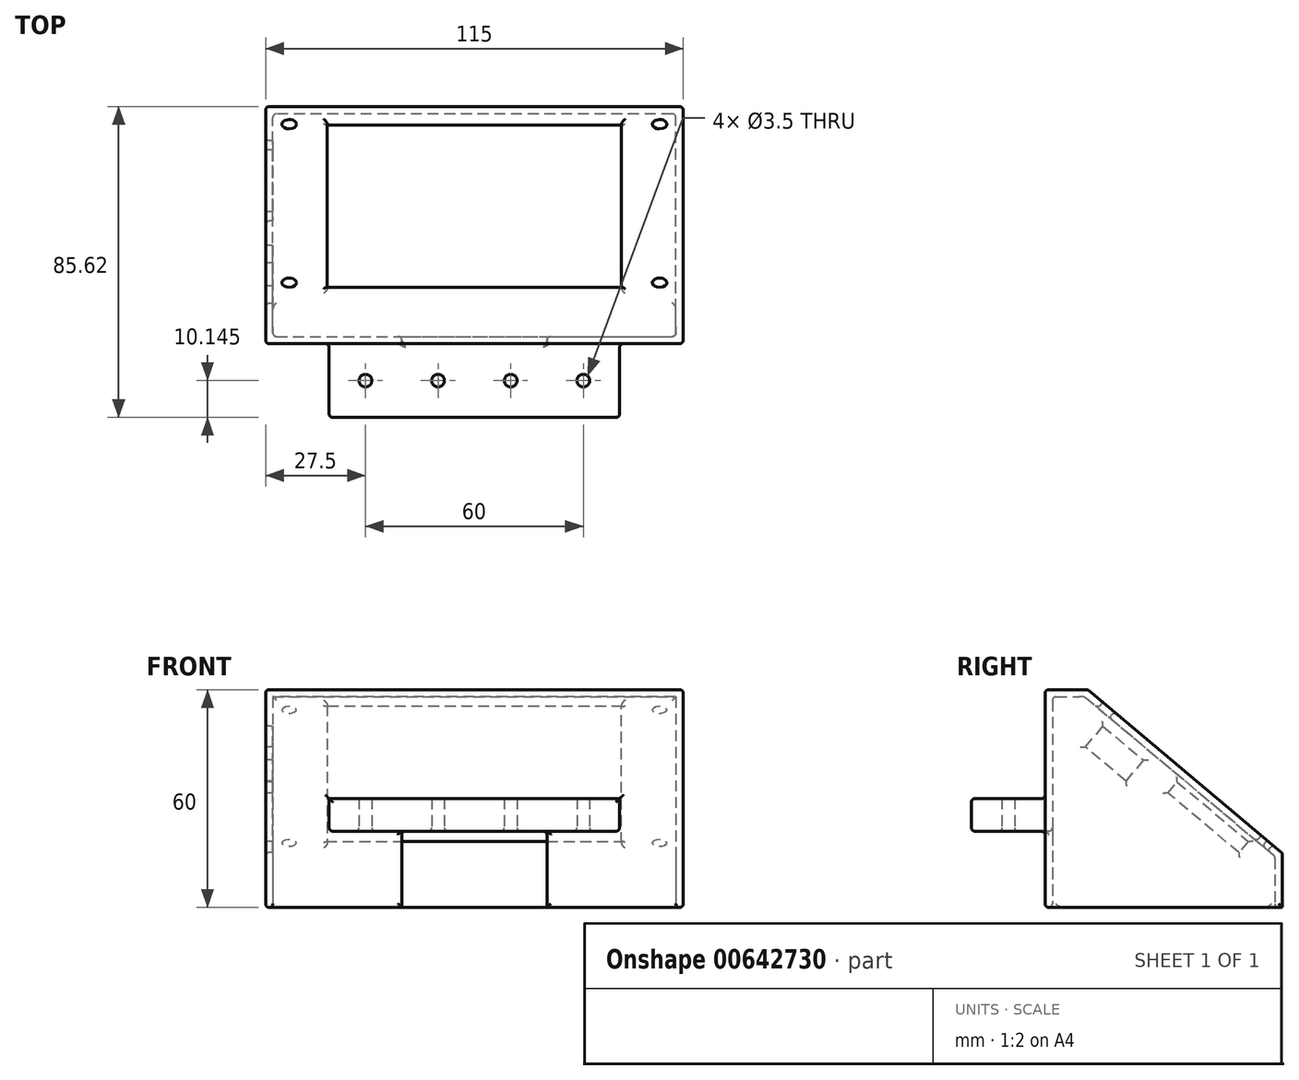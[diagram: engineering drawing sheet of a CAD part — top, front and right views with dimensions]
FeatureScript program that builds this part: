
annotation { "Feature Type Name" : "Feature", "Feature Type Description" : "" }
export const myFeature = defineFeature(function(context is Context, id is Id, definition is map)
    precondition{}
    {
        {
            var Q0;
            Q0=qCreatedBy(makeId("Right.planeOp"),FACE);
            var sketch = newSketch(context, id + "F0", { "sketchPlane" : qUnion([Q0])});
            skLineSegment(sketch, "E0.bottom", {"start": v(-40.36, -2.42) * mm, "end": v(-8.36, -2.42) * mm});
            skLineSegment(sketch, "E0.top", {"start": v(-40.36, -62.42) * mm, "end": v(45.26, -62.42) * mm});
            skLineSegment(sketch, "E0.left", {"start": v(-40.36, -2.42) * mm, "end": v(-40.36, -62.42) * mm});
            skLineSegment(sketch, "E0.right", {"start": v(45.26, -47.41) * mm, "end": v(45.26, -62.42) * mm});
            skLineSegment(sketch, "E1", {"start": v(-8.36, -2.42) * mm, "end": v(45.26, -47.41) * mm});
            skLineSegment(sketch, "E2.bottom", {"start": v(-40.36, -12.12) * mm, "end": v(-20.06, -12.12) * mm});
            skLineSegment(sketch, "E2.top", {"start": v(-40.36, -32.42) * mm, "end": v(-20.06, -32.42) * mm});
            skLineSegment(sketch, "E2.left", {"start": v(-40.36, -12.12) * mm, "end": v(-40.36, -32.42) * mm});
            skLineSegment(sketch, "E2.right", {"start": v(-20.06, -12.12) * mm, "end": v(-20.06, -32.42) * mm});
            skSolve(sketch);
        }
        {
            var Q0;
            {var subQ4=sQuery(id+"F0.wireOp",EDGE,"E0.bottom");Q0=makeQuery(id+"F0.imprint","IMPRINT",FACE,{"disambiguationData":[TD([[makeQuery(id+"F0.imprint","IMPRINT",EDGE,{"derivedFrom":subQ4}),-1.0]])]});}
            extrude(context, id + "F1", {"entities" : qUnion([Q0]), "depth" : 115 * mm, "offsetDistance" : 25 * mm});
        }
        {
            var Q0;
            Q0=makeQuery(id+"F1.opExtrude","CAP_FACE",FACE,{"disambiguationData":[OSD([sQuery(id+"F0.wireOp",EDGE,"E0.bottom"),sQuery(id+"F0.wireOp",EDGE,"E0.top"),sQuery(id+"F0.wireOp",EDGE,"E0.left"),sQuery(id+"F0.wireOp",EDGE,"E0.right"),sQuery(id+"F0.wireOp",EDGE,"E1"),sQuery(id+"F0.wireOp",EDGE,"E2.bottom"),sQuery(id+"F0.wireOp",EDGE,"E2.top"),sQuery(id+"F0.wireOp",EDGE,"E2.right")])],"isStart":false});
            var sketch = newSketch(context, id + "F2", { "sketchPlane" : qUnion([Q0])});
            skLineSegment(sketch, "E3", {"start": v(-20.06, -12.12) * mm, "end": v(-20.06, -2.42) * mm});
            skLineSegment(sketch, "E4", {"start": v(-20.06, -32.42) * mm, "end": v(-20.06, -62.42) * mm});
            skSolve(sketch);
        }
        {
            var Q0;
            {var subQ0=sQuery(id+"F2.wireOp",EDGE,"E3");Q0=makeQuery(id+"F2.imprint","IMPRINT",FACE,{"disambiguationData":[TD([[makeQuery(id+"F2.imprint","IMPRINT",EDGE,{"derivedFrom":subQ0}),1.0]])]});}
            var Q1;
            {var subQ0=sQuery(id+"F2.wireOp",EDGE,"E4");Q1=makeQuery(id+"F2.imprint","IMPRINT",FACE,{"disambiguationData":[TD([[makeQuery(id+"F2.imprint","IMPRINT",EDGE,{"derivedFrom":subQ0}),-1.0]])]});}
            extrude(context, id + "F3", {"entities" : qUnion([Q0, Q1]), "operationType" : NewBodyOperationType.REMOVE, "oppositeDirection" : true, "depth" : 17.5 * mm, "offsetDistance" : 25 * mm});
        }
        {
            var Q0;
            Q0=makeQuery(id+"F1.opExtrude","CAP_FACE",FACE,{"disambiguationData":[OSD([sQuery(id+"F0.wireOp",EDGE,"E0.bottom"),sQuery(id+"F0.wireOp",EDGE,"E0.top"),sQuery(id+"F0.wireOp",EDGE,"E0.left"),sQuery(id+"F0.wireOp",EDGE,"E0.right"),sQuery(id+"F0.wireOp",EDGE,"E1"),sQuery(id+"F0.wireOp",EDGE,"E2.bottom"),sQuery(id+"F0.wireOp",EDGE,"E2.top"),sQuery(id+"F0.wireOp",EDGE,"E2.right")])],"isStart":true});
            var sketch = newSketch(context, id + "F4", { "sketchPlane" : qUnion([Q0])});
            skLineSegment(sketch, "E5", {"start": v(20.06, -12.12) * mm, "end": v(20.06, -2.42) * mm});
            skLineSegment(sketch, "E6", {"start": v(20.06, -32.42) * mm, "end": v(20.06, -62.42) * mm});
            skSolve(sketch);
        }
        {
            var Q0;
            {var subQ0=sQuery(id+"F4.wireOp",EDGE,"E5");Q0=makeQuery(id+"F4.imprint","IMPRINT",FACE,{"disambiguationData":[TD([[makeQuery(id+"F4.imprint","IMPRINT",EDGE,{"derivedFrom":subQ0}),-1.0]])]});}
            var Q1;
            {var subQ0=sQuery(id+"F4.wireOp",EDGE,"E6");Q1=makeQuery(id+"F4.imprint","IMPRINT",FACE,{"disambiguationData":[TD([[makeQuery(id+"F4.imprint","IMPRINT",EDGE,{"derivedFrom":subQ0}),1.0]])]});}
            extrude(context, id + "F5", {"entities" : qUnion([Q0, Q1]), "operationType" : NewBodyOperationType.REMOVE, "oppositeDirection" : true, "depth" : 17.5 * mm, "offsetDistance" : 25 * mm});
        }
        {
            var Q0;
            Q0=makeQuery(id+"F1.opExtrude","SWEPT_FACE",FACE,{"disambiguationData":[OSD([sQuery(id+"F0.wireOp",EDGE,"E0.top")])]});
            var sketch = newSketch(context, id + "F6", { "sketchPlane" : qUnion([Q0])});
            skLineSegment(sketch, "E7", {"start": v(17.5, 20.06) * mm, "end": v(97.5, 20.06) * mm});
            skSolve(sketch);
        }
        {
            var Q0;
            Q0=makeQuery(id+"F6.imprint","IMPRINT",FACE,{"disambiguationData":[TD([[makeQuery(id+"F6.imprint","IMPRINT",EDGE,{"derivedFrom":sQuery(id+"F6.wireOp",EDGE,"E7")}),1.0]])]});
            extrude(context, id + "F7", {"entities" : qUnion([Q0]), "operationType" : NewBodyOperationType.REMOVE, "oppositeDirection" : true, "depth" : 21 * mm, "offsetDistance" : 25 * mm});
        }
        {
            var Q0;
            Q0=makeQuery(id+"F1.opExtrude","SWEPT_FACE",FACE,{"disambiguationData":[OSD([sQuery(id+"F0.wireOp",EDGE,"E0.top")])]});
            shell(context, id + "F8", {"entities" : qUnion([Q0]), "thickness" : 2 * mm});
        }
        {
            var Q0;
            {var subQ0=sQuery(id+"F0.wireOp",EDGE,"E0.left");Q0=makeQuery(id+"F1.opExtrude","SWEPT_FACE",FACE,{"disambiguationData":[OSD([subQ0]),TDD([makeQuery(id+"F0.imprint","IMPRINT",EDGE,{"disambiguationData":[TD([[makeQuery(id+"F0.imprint","INTERSECT",VERTEX,{"derivedFrom":[sQuery(id+"F0.wireOp",EDGE,"E0.bottom"),subQ0]}),-1.0]])],"derivedFrom":subQ0})])]});}
            var Q1;
            {var subQ0=sQuery(id+"F0.wireOp",EDGE,"E0.left");Q1=makeQuery(id+"F1.opExtrude","SWEPT_FACE",FACE,{"disambiguationData":[OSD([subQ0]),TDD([makeQuery(id+"F0.imprint","IMPRINT",EDGE,{"disambiguationData":[TD([[makeQuery(id+"F0.imprint","INTERSECT",VERTEX,{"derivedFrom":[sQuery(id+"F0.wireOp",EDGE,"E0.top"),subQ0]}),1.0]])],"derivedFrom":subQ0})])]});}
            var Q2;
            Q2=makeQuery(id+"F8.opShell","OFFSET_FACE",FACE,{"disambiguationData":[OSD([sQuery(id+"F0.wireOp",EDGE,"E2.right"),sQuery(id+"F2.wireOp",EDGE,"E3"),sQuery(id+"F2.wireOp",EDGE,"E4"),sQuery(id+"F4.wireOp",EDGE,"E5"),sQuery(id+"F4.wireOp",EDGE,"E6"),sQuery(id+"F6.wireOp",EDGE,"E7")])]});
            extrude(context, id + "F9", {"entities" : qUnion([Q0, Q1]), "operationType" : NewBodyOperationType.ADD, "endBound" : BoundingType.UP_TO_SURFACE, "oppositeDirection" : true, "depth" : 25 * mm, "endBoundEntityFace" : qUnion([Q2]), "offsetDistance" : 25 * mm});
        }
        {
            var Q0;
            Q0=makeQuery(id+"F7.boolean.opBoolean","MERGE",FACE,{"derivedFrom":[makeQuery(id+"F5.boolean.opBoolean","MERGE",FACE,{"derivedFrom":[makeQuery(id+"F3.boolean.opBoolean","MERGE",FACE,{"derivedFrom":[makeQuery(id+"F1.opExtrude","SWEPT_FACE",FACE,{"disambiguationData":[OSD([sQuery(id+"F0.wireOp",EDGE,"E2.right")])]}),makeQuery(id+"F3.opExtrude","SWEPT_FACE",FACE,{"disambiguationData":[OSD([sQuery(id+"F2.wireOp",EDGE,"E3")])]}),makeQuery(id+"F3.opExtrude","SWEPT_FACE",FACE,{"disambiguationData":[OSD([sQuery(id+"F2.wireOp",EDGE,"E4")])]})]}),makeQuery(id+"F5.opExtrude","SWEPT_FACE",FACE,{"disambiguationData":[OSD([sQuery(id+"F4.wireOp",EDGE,"E5")])]}),makeQuery(id+"F5.opExtrude","SWEPT_FACE",FACE,{"disambiguationData":[OSD([sQuery(id+"F4.wireOp",EDGE,"E6")])]})]}),makeQuery(id+"F7.opExtrude","SWEPT_FACE",FACE,{"disambiguationData":[OSD([sQuery(id+"F6.wireOp",EDGE,"E7")])]})]});
            var sketch = newSketch(context, id + "F10", { "sketchPlane" : qUnion([Q0])});
            skLineSegment(sketch, "E8.bottom", {"start": v(77.5, -41.42) * mm, "end": v(37.5, -41.42) * mm});
            skLineSegment(sketch, "E8.top", {"start": v(77.5, -83.42) * mm, "end": v(37.5, -83.42) * mm});
            skLineSegment(sketch, "E8.left", {"start": v(77.5, -41.42) * mm, "end": v(77.5, -83.42) * mm});
            skLineSegment(sketch, "E8.right", {"start": v(37.5, -41.42) * mm, "end": v(37.5, -83.42) * mm});
            skPoint(sketch, "E8.middle", {"position": v(57.5, -62.42) * mm});
            skSolve(sketch);
        }
        {
            var Q0;
            {var subQ0=sQuery(id+"F10.wireOp",EDGE,"E8.bottom");Q0=makeQuery(id+"F10.imprint","IMPRINT",FACE,{"disambiguationData":[TD([[makeQuery(id+"F10.imprint","IMPRINT",EDGE,{"derivedFrom":subQ0}),-1.0]])]});}
            extrude(context, id + "F11", {"entities" : qUnion([Q0]), "operationType" : NewBodyOperationType.REMOVE, "endBound" : BoundingType.UP_TO_NEXT, "oppositeDirection" : true, "depth" : 25 * mm, "offsetDistance" : 25 * mm});
        }
        {
            var Q0;
            Q0=makeQuery(id+"F1.opExtrude","SWEPT_FACE",FACE,{"disambiguationData":[OSD([sQuery(id+"F0.wireOp",EDGE,"E1")])]});
            var sketch = newSketch(context, id + "F12", { "sketchPlane" : qUnion([Q0])});
            skLineSegment(sketch, "E9.bottom", {"start": v(112.5, 63.15) * mm, "end": v(2.5, 63.15) * mm, "construction": true});
            skLineSegment(sketch, "E9.top", {"start": v(112.5, -1.85) * mm, "end": v(2.5, -1.85) * mm, "construction": true});
            skLineSegment(sketch, "E9.left", {"start": v(112.5, 63.15) * mm, "end": v(112.5, -1.85) * mm, "construction": true});
            skLineSegment(sketch, "E9.right", {"start": v(2.5, 63.15) * mm, "end": v(2.5, -1.85) * mm, "construction": true});
            skCircle(sketch, "E10", {"center": v(108.5, 59.65) * mm, "radius": 2 * mm});
            skCircle(sketch, "E11.0.1.0", {"center": v(108.5, 2.65) * mm, "radius": 2 * mm});
            skCircle(sketch, "E11.1.0.0", {"center": v(6.5, 59.65) * mm, "radius": 2 * mm});
            skCircle(sketch, "E11.1.1.0", {"center": v(6.5, 2.65) * mm, "radius": 2 * mm});
            skLineSegment(sketch, "E11.direction1", {"start": v(108.5, 59.65) * mm, "end": v(6.5, 59.65) * mm, "construction": true});
            skLineSegment(sketch, "E11.direction2", {"start": v(108.5, 59.65) * mm, "end": v(108.5, 2.65) * mm, "construction": true});
            skLineSegment(sketch, "E12.bottom", {"start": v(98, 59.65) * mm, "end": v(17, 59.65) * mm});
            skLineSegment(sketch, "E12.top", {"start": v(98, 0.65) * mm, "end": v(17, 0.65) * mm});
            skLineSegment(sketch, "E12.left", {"start": v(98, 59.65) * mm, "end": v(98, 0.65) * mm});
            skLineSegment(sketch, "E12.right", {"start": v(17, 59.65) * mm, "end": v(17, 0.65) * mm});
            skSolve(sketch);
        }
        {
            var Q0;
            Q0=makeQuery(id+"F12.imprint","IMPRINT",FACE,{"disambiguationData":[TD([[makeQuery(id+"F12.imprint","IMPRINT",EDGE,{"derivedFrom":sQuery(id+"F12.wireOp",EDGE,"E12.bottom")}),1.0]])]});
            var Q1;
            Q1=makeQuery(id+"F12.imprint","IMPRINT",FACE,{"disambiguationData":[TD([[makeQuery(id+"F12.imprint","IMPRINT",EDGE,{"derivedFrom":sQuery(id+"F12.wireOp",EDGE,"E10")}),1.0]])]});
            var Q2;
            Q2=makeQuery(id+"F12.imprint","IMPRINT",FACE,{"disambiguationData":[TD([[makeQuery(id+"F12.imprint","IMPRINT",EDGE,{"derivedFrom":sQuery(id+"F12.wireOp",EDGE,"E11.0.1.0")}),1.0]])]});
            var Q3;
            Q3=makeQuery(id+"F12.imprint","IMPRINT",FACE,{"disambiguationData":[TD([[makeQuery(id+"F12.imprint","IMPRINT",EDGE,{"derivedFrom":sQuery(id+"F12.wireOp",EDGE,"E11.1.0.0")}),1.0]])]});
            var Q4;
            Q4=makeQuery(id+"F12.imprint","IMPRINT",FACE,{"disambiguationData":[TD([[makeQuery(id+"F12.imprint","IMPRINT",EDGE,{"derivedFrom":sQuery(id+"F12.wireOp",EDGE,"E11.1.1.0")}),1.0]])]});
            extrude(context, id + "F13", {"entities" : qUnion([Q0, Q1, Q2, Q3, Q4]), "operationType" : NewBodyOperationType.REMOVE, "endBound" : BoundingType.UP_TO_NEXT, "oppositeDirection" : true, "depth" : 25 * mm, "offsetDistance" : 25 * mm});
        }
        {
            var Q0;
            Q0=makeQuery(id+"F11.boolean.opBoolean","MERGE",FACE,{"derivedFrom":[makeQuery(id+"F7.boolean.opBoolean","COPY",FACE,{"derivedFrom":makeQuery(id+"F7.opExtrude","CAP_FACE",FACE,{"disambiguationData":[OSD([sQuery(id+"F0.wireOp",EDGE,"E0.top"),sQuery(id+"F0.wireOp",EDGE,"E0.left"),sQuery(id+"F6.wireOp",EDGE,"E7")])],"isStart":false})}),makeQuery(id+"F11.opExtrude","SWEPT_FACE",FACE,{"disambiguationData":[OSD([sQuery(id+"F10.wireOp",EDGE,"E8.bottom")])]})]});
            var sketch = newSketch(context, id + "F14", { "sketchPlane" : qUnion([Q0])});
            skLineSegment(sketch, "E13.bottom", {"start": v(97.5, 40.36) * mm, "end": v(17.5, 40.36) * mm, "construction": true});
            skLineSegment(sketch, "E13.top", {"start": v(97.5, 20.06) * mm, "end": v(17.5, 20.06) * mm, "construction": true});
            skLineSegment(sketch, "E13.left", {"start": v(97.5, 40.36) * mm, "end": v(97.5, 20.06) * mm, "construction": true});
            skLineSegment(sketch, "E13.right", {"start": v(17.5, 40.36) * mm, "end": v(17.5, 20.06) * mm, "construction": true});
            skLineSegment(sketch, "E14.bottom", {"start": v(17.5, 40.36) * mm, "end": v(57.5, 40.36) * mm, "construction": true});
            skLineSegment(sketch, "E14.top", {"start": v(17.5, 20.06) * mm, "end": v(57.5, 20.06) * mm, "construction": true});
            skLineSegment(sketch, "E14.right", {"start": v(57.5, 40.36) * mm, "end": v(57.5, 20.06) * mm, "construction": true});
            skLineSegment(sketch, "E15.bottom", {"start": v(57.5, 40.36) * mm, "end": v(37.5, 40.36) * mm, "construction": true});
            skLineSegment(sketch, "E15.top", {"start": v(57.5, 20.06) * mm, "end": v(37.5, 20.06) * mm, "construction": true});
            skLineSegment(sketch, "E15.right", {"start": v(37.5, 40.36) * mm, "end": v(37.5, 20.06) * mm, "construction": true});
            skCircle(sketch, "E16", {"center": v(27.5, 30.21) * mm, "radius": 1.75 * mm});
            skPoint(sketch, "E16.centerSnap0", {"position": v(27.5, 20.06) * mm});
            skPoint(sketch, "E16.centerSnap1", {"position": v(17.5, 30.21) * mm});
            skCircle(sketch, "E17.1.0.0", {"center": v(47.5, 30.21) * mm, "radius": 1.75 * mm});
            skCircle(sketch, "E17.2.0.0", {"center": v(67.5, 30.21) * mm, "radius": 1.75 * mm});
            skCircle(sketch, "E17.3.0.0", {"center": v(87.5, 30.21) * mm, "radius": 1.75 * mm});
            skLineSegment(sketch, "E17.direction1", {"start": v(27.5, 30.21) * mm, "end": v(47.5, 30.21) * mm, "construction": true});
            skSolve(sketch);
        }
        {
            var Q0;
            Q0=makeQuery(id+"F14.imprint","IMPRINT",FACE,{"disambiguationData":[TD([[makeQuery(id+"F14.imprint","IMPRINT",EDGE,{"derivedFrom":sQuery(id+"F14.wireOp",EDGE,"E17.3.0.0")}),1.0]])]});
            var Q1;
            Q1=makeQuery(id+"F14.imprint","IMPRINT",FACE,{"disambiguationData":[TD([[makeQuery(id+"F14.imprint","IMPRINT",EDGE,{"derivedFrom":sQuery(id+"F14.wireOp",EDGE,"E17.2.0.0")}),1.0]])]});
            var Q2;
            Q2=makeQuery(id+"F14.imprint","IMPRINT",FACE,{"disambiguationData":[TD([[makeQuery(id+"F14.imprint","IMPRINT",EDGE,{"derivedFrom":sQuery(id+"F14.wireOp",EDGE,"E17.1.0.0")}),1.0]])]});
            var Q3;
            Q3=makeQuery(id+"F14.imprint","IMPRINT",FACE,{"disambiguationData":[TD([[makeQuery(id+"F14.imprint","IMPRINT",EDGE,{"derivedFrom":sQuery(id+"F14.wireOp",EDGE,"E16")}),1.0]])]});
            var Q4;
            Q4=makeQuery(id+"F1.opExtrude","SWEPT_FACE",FACE,{"disambiguationData":[OSD([sQuery(id+"F0.wireOp",EDGE,"E0.bottom")])]});
            extrude(context, id + "F15", {"entities" : qUnion([Q0, Q1, Q2, Q3]), "operationType" : NewBodyOperationType.REMOVE, "endBound" : BoundingType.UP_TO_SURFACE, "oppositeDirection" : true, "depth" : 25 * mm, "endBoundEntityFace" : qUnion([Q4]), "offsetDistance" : 25 * mm});
        }
        {
            var Q0;
            Q0=makeQuery(id+"F1.opExtrude","CAP_FACE",FACE,{"disambiguationData":[OSD([sQuery(id+"F0.wireOp",EDGE,"E0.bottom"),sQuery(id+"F0.wireOp",EDGE,"E0.top"),sQuery(id+"F0.wireOp",EDGE,"E0.left"),sQuery(id+"F0.wireOp",EDGE,"E0.right"),sQuery(id+"F0.wireOp",EDGE,"E1"),sQuery(id+"F0.wireOp",EDGE,"E2.bottom"),sQuery(id+"F0.wireOp",EDGE,"E2.top"),sQuery(id+"F0.wireOp",EDGE,"E2.right")])],"isStart":true});
            var sketch = newSketch(context, id + "F16", { "sketchPlane" : qUnion([Q0])});
            skLineSegment(sketch, "E18", {"start": v(-33.28, -47.28) * mm, "end": v(-13.74, -30.89) * mm});
            skLineSegment(sketch, "E19", {"start": v(-13.74, -30.89) * mm, "end": v(-16.31, -27.83) * mm});
            skLineSegment(sketch, "E20", {"start": v(-16.31, -27.83) * mm, "end": v(-35.85, -44.22) * mm});
            skLineSegment(sketch, "E21", {"start": v(-35.85, -44.22) * mm, "end": v(-33.28, -47.28) * mm});
            skLineSegment(sketch, "E22", {"start": v(-6.99, -21.83) * mm, "end": v(-2.17, -27.57) * mm});
            skLineSegment(sketch, "E23", {"start": v(-2.17, -27.57) * mm, "end": v(8.94, -18.25) * mm});
            skLineSegment(sketch, "E24", {"start": v(8.94, -18.25) * mm, "end": v(4.12, -12.5) * mm});
            skLineSegment(sketch, "E25", {"start": v(4.12, -12.5) * mm, "end": v(-6.99, -21.83) * mm});
            skSolve(sketch);
        }
        {
            var Q0;
            Q0=makeQuery(id+"F16.imprint","IMPRINT",FACE,{"disambiguationData":[TD([[makeQuery(id+"F16.imprint","IMPRINT",EDGE,{"derivedFrom":sQuery(id+"F16.wireOp",EDGE,"E22")}),1.0]])]});
            var Q1;
            Q1=makeQuery(id+"F16.imprint","IMPRINT",FACE,{"disambiguationData":[TD([[makeQuery(id+"F16.imprint","IMPRINT",EDGE,{"derivedFrom":sQuery(id+"F16.wireOp",EDGE,"E18")}),1.0]])]});
            extrude(context, id + "F17", {"entities" : qUnion([Q0, Q1]), "operationType" : NewBodyOperationType.REMOVE, "endBound" : BoundingType.UP_TO_NEXT, "oppositeDirection" : true, "depth" : 25 * mm, "offsetDistance" : 25 * mm});
        }
        {
            var Q0;
            Q0=makeQuery(id+"F1.opExtrude","SWEPT_FACE",FACE,{"disambiguationData":[OSD([sQuery(id+"F0.wireOp",EDGE,"E1")])]});
            var Q1;
            Q1=makeQuery(id+"F1.opExtrude","CAP_FACE",FACE,{"disambiguationData":[OSD([sQuery(id+"F0.wireOp",EDGE,"E0.bottom"),sQuery(id+"F0.wireOp",EDGE,"E0.top"),sQuery(id+"F0.wireOp",EDGE,"E0.left"),sQuery(id+"F0.wireOp",EDGE,"E0.right"),sQuery(id+"F0.wireOp",EDGE,"E1"),sQuery(id+"F0.wireOp",EDGE,"E2.bottom"),sQuery(id+"F0.wireOp",EDGE,"E2.top"),sQuery(id+"F0.wireOp",EDGE,"E2.right")])],"isStart":false});
            var Q2;
            Q2=makeQuery(id+"F11.boolean.opBoolean","MERGE",FACE,{"derivedFrom":[makeQuery(id+"F7.boolean.opBoolean","COPY",FACE,{"derivedFrom":makeQuery(id+"F7.opExtrude","CAP_FACE",FACE,{"disambiguationData":[OSD([sQuery(id+"F0.wireOp",EDGE,"E0.top"),sQuery(id+"F0.wireOp",EDGE,"E0.left"),sQuery(id+"F6.wireOp",EDGE,"E7")])],"isStart":false})}),makeQuery(id+"F11.opExtrude","SWEPT_FACE",FACE,{"disambiguationData":[OSD([sQuery(id+"F10.wireOp",EDGE,"E8.bottom")])]})]});
            var Q3;
            {var subQ0=sQuery(id+"F0.wireOp",EDGE,"E0.left");Q3=makeQuery(id+"F1.opExtrude","SWEPT_FACE",FACE,{"disambiguationData":[OSD([subQ0]),TDD([makeQuery(id+"F0.imprint","IMPRINT",EDGE,{"disambiguationData":[TD([[makeQuery(id+"F0.imprint","INTERSECT",VERTEX,{"derivedFrom":[sQuery(id+"F0.wireOp",EDGE,"E0.top"),subQ0]}),1.0]])],"derivedFrom":subQ0})])]});}
            var Q4;
            Q4=makeQuery(id+"F8.opShell","OFFSET_FACE",FACE,{"disambiguationData":[OSD([sQuery(id+"F0.wireOp",EDGE,"E1")])]});
            var Q5;
            Q5=makeQuery(id+"F8.opShell","OFFSET_FACE",FACE,{"disambiguationData":[OSD([sQuery(id+"F0.wireOp",EDGE,"E0.right")])]});
            var Q6;
            {var subQ0=sQuery(id+"F6.wireOp",EDGE,"E7");var subQ1=sQuery(id+"F4.wireOp",EDGE,"E6");var subQ2=sQuery(id+"F4.wireOp",EDGE,"E5");var subQ3=sQuery(id+"F2.wireOp",EDGE,"E4");var subQ4=sQuery(id+"F2.wireOp",EDGE,"E3");var subQ5=sQuery(id+"F0.wireOp",EDGE,"E2.right");Q6=makeQuery(id+"F9.boolean.opBoolean","MERGE",FACE,{"derivedFrom":[makeQuery(id+"F8.opShell","OFFSET_FACE",FACE,{"disambiguationData":[OSD([subQ5,subQ4,subQ3,subQ2,subQ1,subQ0])]}),makeQuery(id+"F9.opExtrude","CAP_FACE",FACE,{"disambiguationData":[OSD([subQ5,subQ4,subQ3,subQ2,subQ1,subQ0]),OD(0.0)],"isStart":false}),makeQuery(id+"F9.opExtrude","CAP_FACE",FACE,{"disambiguationData":[OSD([subQ5,subQ4,subQ3,subQ2,subQ1,subQ0]),OD(1.0)],"isStart":false})]});}
            var Q7;
            Q7=makeQuery(id+"F1.opExtrude","CAP_FACE",FACE,{"disambiguationData":[OSD([sQuery(id+"F0.wireOp",EDGE,"E0.bottom"),sQuery(id+"F0.wireOp",EDGE,"E0.top"),sQuery(id+"F0.wireOp",EDGE,"E0.left"),sQuery(id+"F0.wireOp",EDGE,"E0.right"),sQuery(id+"F0.wireOp",EDGE,"E1"),sQuery(id+"F0.wireOp",EDGE,"E2.bottom"),sQuery(id+"F0.wireOp",EDGE,"E2.top"),sQuery(id+"F0.wireOp",EDGE,"E2.right")])],"isStart":true});
            fillet(context, id + "F18", {"entities" : qUnion([Q0, Q1, Q2, Q3, Q4, Q5, Q6, Q7]), "radius" : 1 * mm, "tangentPropagation" : true, "allowEdgeOverflow" : false});
        }
        {
            var Q0;
            Q0=makeQuery(id+"F5.boolean.opBoolean","COPY",FACE,{"derivedFrom":makeQuery(id+"F5.opExtrude","CAP_FACE",FACE,{"disambiguationData":[OSD([sQuery(id+"F0.wireOp",EDGE,"E0.bottom"),sQuery(id+"F0.wireOp",EDGE,"E0.left"),sQuery(id+"F0.wireOp",EDGE,"E2.bottom"),sQuery(id+"F4.wireOp",EDGE,"E5")])],"isStart":false})});
            var Q1;
            Q1=makeQuery(id+"F3.boolean.opBoolean","COPY",FACE,{"derivedFrom":makeQuery(id+"F3.opExtrude","CAP_FACE",FACE,{"disambiguationData":[OSD([sQuery(id+"F0.wireOp",EDGE,"E0.bottom"),sQuery(id+"F0.wireOp",EDGE,"E0.left"),sQuery(id+"F0.wireOp",EDGE,"E2.bottom"),sQuery(id+"F2.wireOp",EDGE,"E3")])],"isStart":false})});
            extrude(context, id + "F19", {"entities" : qUnion([Q0, Q1]), "operationType" : NewBodyOperationType.REMOVE, "oppositeDirection" : true, "depth" : 94.52 * mm, "offsetDistance" : 25 * mm});
        }
        {
            var Q0;
            {var subQ0=sQuery(id+"F4.wireOp",EDGE,"E5");var subQ1=sQuery(id+"F2.wireOp",EDGE,"E3");Q0=makeQuery(id+"F19.boolean.opBoolean","MERGE",FACE,{"derivedFrom":[makeQuery(id+"F7.boolean.opBoolean","MERGE",FACE,{"derivedFrom":[makeQuery(id+"F5.boolean.opBoolean","MERGE",FACE,{"derivedFrom":[makeQuery(id+"F3.boolean.opBoolean","MERGE",FACE,{"derivedFrom":[makeQuery(id+"F1.opExtrude","SWEPT_FACE",FACE,{"disambiguationData":[OSD([sQuery(id+"F0.wireOp",EDGE,"E2.right")])]}),makeQuery(id+"F3.opExtrude","SWEPT_FACE",FACE,{"disambiguationData":[OSD([subQ1])]}),makeQuery(id+"F3.opExtrude","SWEPT_FACE",FACE,{"disambiguationData":[OSD([sQuery(id+"F2.wireOp",EDGE,"E4")])]})]}),makeQuery(id+"F5.opExtrude","SWEPT_FACE",FACE,{"disambiguationData":[OSD([subQ0])]}),makeQuery(id+"F5.opExtrude","SWEPT_FACE",FACE,{"disambiguationData":[OSD([sQuery(id+"F4.wireOp",EDGE,"E6")])]})]}),makeQuery(id+"F7.opExtrude","SWEPT_FACE",FACE,{"disambiguationData":[OSD([sQuery(id+"F6.wireOp",EDGE,"E7")])]})]}),makeQuery(id+"F19.opExtrude","SWEPT_FACE",FACE,{"disambiguationData":[OSD([subQ1])]}),makeQuery(id+"F19.opExtrude","SWEPT_FACE",FACE,{"disambiguationData":[OSD([subQ0])]})]});}
            fillet(context, id + "F20", {"entities" : qUnion([Q0]), "radius" : 1 * mm, "tangentPropagation" : true, "allowEdgeOverflow" : false});
        }
    });
